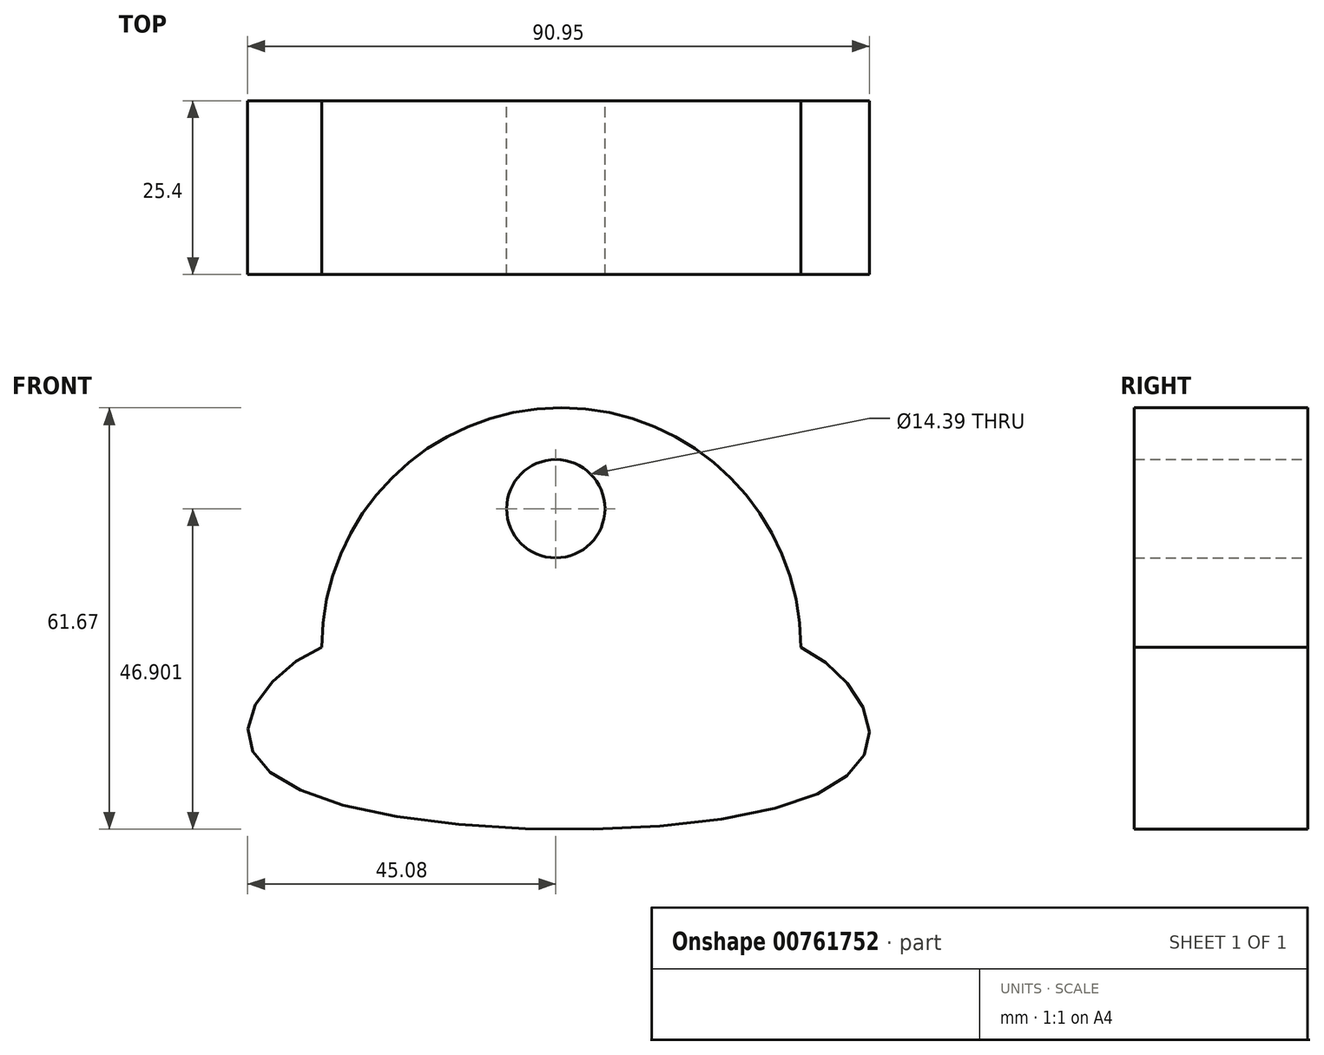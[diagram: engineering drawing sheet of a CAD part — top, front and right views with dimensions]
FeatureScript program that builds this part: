
annotation { "Feature Type Name" : "Feature", "Feature Type Description" : "" }
export const myFeature = defineFeature(function(context is Context, id is Id, definition is map)
    precondition{}
    {
        {
            var Q0;
            Q0=qCreatedBy(makeId("Front.planeOp"),FACE);
            var sketch = newSketch(context, id + "F0", { "sketchPlane" : qUnion([Q0])});
            skArc(sketch, "E0", {"start": v(35.84, 0) * mm, "mid": v(0.8, 35.04) * mm, "end": v(-34.23, 0) * mm});
            skFitSpline(sketch, "E1", {"points": [v(-34.23, 0) * mm, v(-44.97, -11.14) * mm, v(-34.23, -22.15) * mm, v(35.84, -22.42) * mm, v(45.78, -11.41) * mm, v(35.84, 0) * mm], "startDerivative": vector(-86.6, -34.18) * mm, "endDerivative": vector(-85.45, 39.2) * mm});
            skCircle(sketch, "E2", {"center": v(0, 20.27) * mm, "radius": 7.2 * mm});
            skSolve(sketch);
        }
        {
            var Q0;
            Q0=makeQuery(id+"F0.imprint","IMPRINT",FACE,{"disambiguationData":[TD([[makeQuery(id+"F0.imprint","IMPRINT",EDGE,{"derivedFrom":sQuery(id+"F0.wireOp",EDGE,"E0")}),1.0]])]});
            extrude(context, id + "F1", {"entities" : qUnion([Q0]), "depth" : 25.4 * mm, "offsetDistance" : 25.4 * mm});
        }
    });
